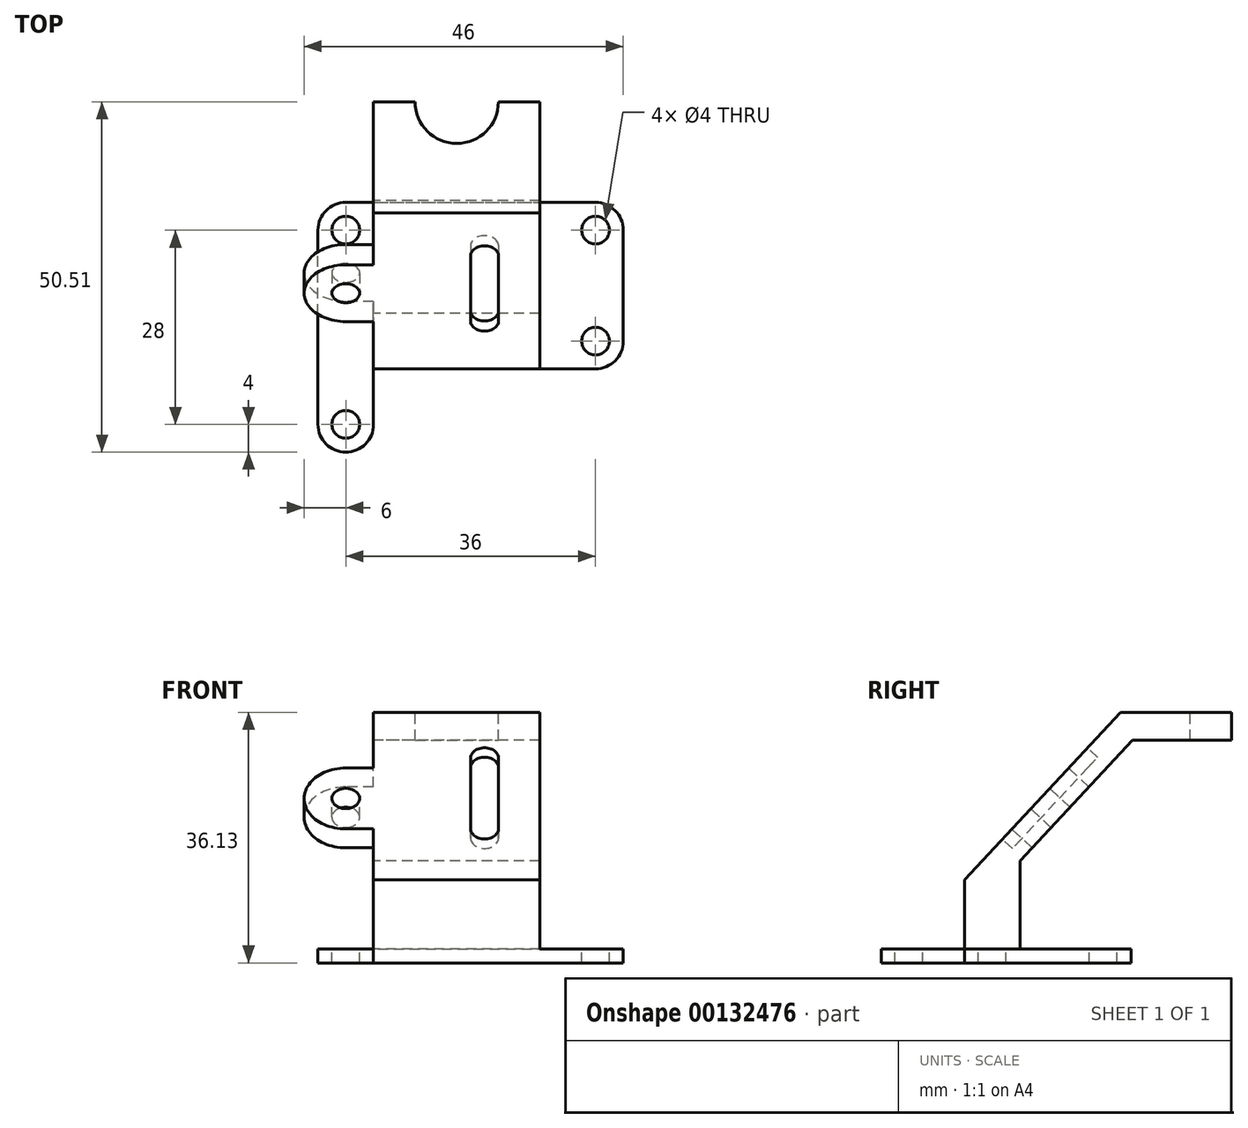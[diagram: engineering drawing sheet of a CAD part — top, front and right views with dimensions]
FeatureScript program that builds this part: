
annotation { "Feature Type Name" : "Feature", "Feature Type Description" : "" }
export const myFeature = defineFeature(function(context is Context, id is Id, definition is map)
    precondition{}
    {
        {
            var Q0;
            Q0=qCreatedBy(makeId("Top.planeOp"),FACE);
            var sketch = newSketch(context, id + "F0", { "sketchPlane" : qUnion([Q0])});
            skLineSegment(sketch, "E0", {"start": v(0, 0) * mm, "end": v(0, 28) * mm});
            skLineSegment(sketch, "E1", {"start": v(4, 32) * mm, "end": v(40, 32) * mm});
            skLineSegment(sketch, "E2", {"start": v(44, 28) * mm, "end": v(44, 12) * mm});
            skLineSegment(sketch, "E3", {"start": v(40, 8) * mm, "end": v(8, 8) * mm});
            skLineSegment(sketch, "E4", {"start": v(8, 8) * mm, "end": v(8, 0) * mm});
            skArc(sketch, "E5", {"start": v(0, 0) * mm, "mid": v(4, -4) * mm, "end": v(8, 0) * mm});
            skPoint(sketch, "E6.visualSharp", {"position": v(44, 32) * mm});
            skArc(sketch, "E6.filletArc", {"start": v(44, 28) * mm, "mid": v(42.83, 30.83) * mm, "end": v(40, 32) * mm});
            skPoint(sketch, "E7.visualSharp", {"position": v(44, 8) * mm});
            skArc(sketch, "E7.filletArc", {"start": v(40, 8) * mm, "mid": v(42.83, 9.17) * mm, "end": v(44, 12) * mm});
            skPoint(sketch, "E8.visualSharp", {"position": v(0, 32) * mm});
            skArc(sketch, "E8.filletArc", {"start": v(4, 32) * mm, "mid": v(1.17, 30.83) * mm, "end": v(0, 28) * mm});
            skSolve(sketch);
        }
        {
            var Q0;
            Q0=makeQuery(id+"F0.imprint","IMPRINT",FACE,{"disambiguationData":[TD([[makeQuery(id+"F0.imprint","IMPRINT",EDGE,{"derivedFrom":sQuery(id+"F0.wireOp",EDGE,"E0")}),-1.0]])]});
            extrude(context, id + "F1", {"entities" : qUnion([Q0]), "oppositeDirection" : true, "depth" : 2 * mm});
        }
        {
            var Q0;
            Q0=makeQuery(id+"F1.opExtrude","SWEPT_FACE",FACE,{"disambiguationData":[OSD([sQuery(id+"F0.wireOp",EDGE,"E4")])]});
            var sketch = newSketch(context, id + "F2", { "sketchPlane" : qUnion([Q0])});
            skLineSegment(sketch, "E9", {"start": v(8, 0) * mm, "end": v(8, 10) * mm});
            skLineSegment(sketch, "E10", {"start": v(8, 10) * mm, "end": v(30.5, 34.13) * mm});
            skLineSegment(sketch, "E11", {"start": v(16, 0) * mm, "end": v(16, 12.71) * mm});
            skLineSegment(sketch, "E12", {"start": v(16, 12.71) * mm, "end": v(32.25, 30.13) * mm});
            skLineSegment(sketch, "E13", {"start": v(32.25, 30.13) * mm, "end": v(46.5, 30.13) * mm});
            skLineSegment(sketch, "E14", {"start": v(30.5, 34.13) * mm, "end": v(46.5, 34.13) * mm});
            skLineSegment(sketch, "E15", {"start": v(46.5, 34.13) * mm, "end": v(46.5, 30.13) * mm});
            skLineSegment(sketch, "E16", {"start": v(16, 12.71) * mm, "end": v(36.2, 12.71) * mm, "construction": true});
            skLineSegment(sketch, "E17", {"start": v(8, 0) * mm, "end": v(16, 0) * mm});
            skSolve(sketch);
        }
        {
            var Q0;
            Q0=makeQuery(id+"F2.imprint","IMPRINT",FACE,{"disambiguationData":[TD([[makeQuery(id+"F2.imprint","IMPRINT",EDGE,{"derivedFrom":sQuery(id+"F2.wireOp",EDGE,"E9")}),-1.0]])]});
            extrude(context, id + "F3", {"entities" : qUnion([Q0]), "operationType" : NewBodyOperationType.ADD, "depth" : 24 * mm});
        }
        {
            var Q0;
            Q0=makeQuery(id+"F1.opExtrude","CAP_FACE",FACE,{"disambiguationData":[OSD([sQuery(id+"F0.wireOp",EDGE,"E0"),sQuery(id+"F0.wireOp",EDGE,"E1"),sQuery(id+"F0.wireOp",EDGE,"E2"),sQuery(id+"F0.wireOp",EDGE,"E3"),sQuery(id+"F0.wireOp",EDGE,"E4"),sQuery(id+"F0.wireOp",EDGE,"E5")])],"isStart":true});
            var sketch = newSketch(context, id + "F4", { "sketchPlane" : qUnion([Q0])});
            skCircle(sketch, "E18", {"center": v(40, 12) * mm, "radius": 2 * mm});
            skCircle(sketch, "E19", {"center": v(40, 28) * mm, "radius": 2 * mm});
            skCircle(sketch, "E20", {"center": v(4, 0) * mm, "radius": 2 * mm});
            skCircle(sketch, "E21", {"center": v(4, 28) * mm, "radius": 2 * mm});
            skSolve(sketch);
        }
        {
            var Q0;
            Q0 = qSketchRegion(id + "F4", true);
            extrude(context, id + "F5", {"entities" : qUnion([Q0]), "operationType" : NewBodyOperationType.REMOVE, "endBound" : BoundingType.THROUGH_ALL, "oppositeDirection" : true, "depth" : 25 * mm});
        }
        {
            var Q0;
            Q0=makeQuery(id+"F3.opExtrude","SWEPT_FACE",FACE,{"disambiguationData":[OSD([sQuery(id+"F2.wireOp",EDGE,"E10")])]});
            var sketch = newSketch(context, id + "F6", { "sketchPlane" : qUnion([Q0])});
            skLineSegment(sketch, "E22.0", {"start": v(8, 12.77) * mm, "end": v(8, 45.77) * mm});
            skLineSegment(sketch, "E23", {"start": v(8, 34.77) * mm, "end": v(4, 34.77) * mm});
            skLineSegment(sketch, "E24", {"start": v(8, 22.77) * mm, "end": v(4, 22.77) * mm});
            skArc(sketch, "E25", {"start": v(4, 34.77) * mm, "mid": v(-2, 28.77) * mm, "end": v(4, 22.77) * mm});
            skCircle(sketch, "E26", {"center": v(4, 28.77) * mm, "radius": 2 * mm});
            skLineSegment(sketch, "E27", {"start": v(26, 36.77) * mm, "end": v(26, 22.77) * mm});
            skLineSegment(sketch, "E28", {"start": v(22, 36.77) * mm, "end": v(22, 22.77) * mm});
            skArc(sketch, "E29", {"start": v(26, 36.77) * mm, "mid": v(24, 38.77) * mm, "end": v(22, 36.77) * mm});
            skArc(sketch, "E30", {"start": v(22, 22.77) * mm, "mid": v(24, 20.77) * mm, "end": v(26, 22.77) * mm});
            skLineSegment(sketch, "E31.0", {"start": v(32, 45.77) * mm, "end": v(8, 45.77) * mm});
            skLineSegment(sketch, "E31.1", {"start": v(32, 12.77) * mm, "end": v(32, 45.77) * mm});
            skLineSegment(sketch, "E31.2", {"start": v(32, 12.77) * mm, "end": v(8, 12.77) * mm});
            skLineSegment(sketch, "E32", {"start": v(8, 22.77) * mm, "end": v(8, 34.77) * mm});
            skSolve(sketch);
        }
        {
            var Q0;
            {var subQ1=sQuery(id+"F6.wireOp",EDGE,"E23");Q0=makeQuery(id+"F6.imprint","IMPRINT",FACE,{"disambiguationData":[TD([[makeQuery(id+"F6.imprint","IMPRINT",EDGE,{"derivedFrom":subQ1}),1.0]])]});}
            extrude(context, id + "F7", {"entities" : qUnion([Q0]), "operationType" : NewBodyOperationType.ADD, "oppositeDirection" : true, "depth" : 4 * mm});
        }
        {
            var Q0;
            Q0=makeQuery(id+"F6.imprint","IMPRINT",FACE,{"disambiguationData":[TD([[makeQuery(id+"F6.imprint","IMPRINT",EDGE,{"derivedFrom":sQuery(id+"F6.wireOp",EDGE,"E27")}),-1.0]])]});
            extrude(context, id + "F8", {"entities" : qUnion([Q0]), "operationType" : NewBodyOperationType.REMOVE, "oppositeDirection" : true, "depth" : 2 * mm});
        }
        {
            var Q0;
            Q0=makeQuery(id+"F3.opExtrude","SWEPT_FACE",FACE,{"disambiguationData":[OSD([sQuery(id+"F2.wireOp",EDGE,"E14")])]});
            var sketch = newSketch(context, id + "F9", { "sketchPlane" : qUnion([Q0])});
            skLineSegment(sketch, "E33.0", {"start": v(32, 46.5) * mm, "end": v(8, 46.5) * mm});
            skArc(sketch, "E34", {"start": v(14, 46.5) * mm, "mid": v(20, 40.5) * mm, "end": v(26, 46.5) * mm});
            skLineSegment(sketch, "E35", {"start": v(14, 46.5) * mm, "end": v(26, 46.5) * mm});
            skSolve(sketch);
        }
        {
            var Q0;
            Q0=makeQuery(id+"F9.imprint","IMPRINT",FACE,{"disambiguationData":[TD([[makeQuery(id+"F9.imprint","IMPRINT",EDGE,{"derivedFrom":sQuery(id+"F9.wireOp",EDGE,"E34")}),1.0]])]});
            extrude(context, id + "F10", {"entities" : qUnion([Q0]), "operationType" : NewBodyOperationType.REMOVE, "endBound" : BoundingType.THROUGH_ALL, "oppositeDirection" : true, "depth" : 25 * mm});
        }
    });
